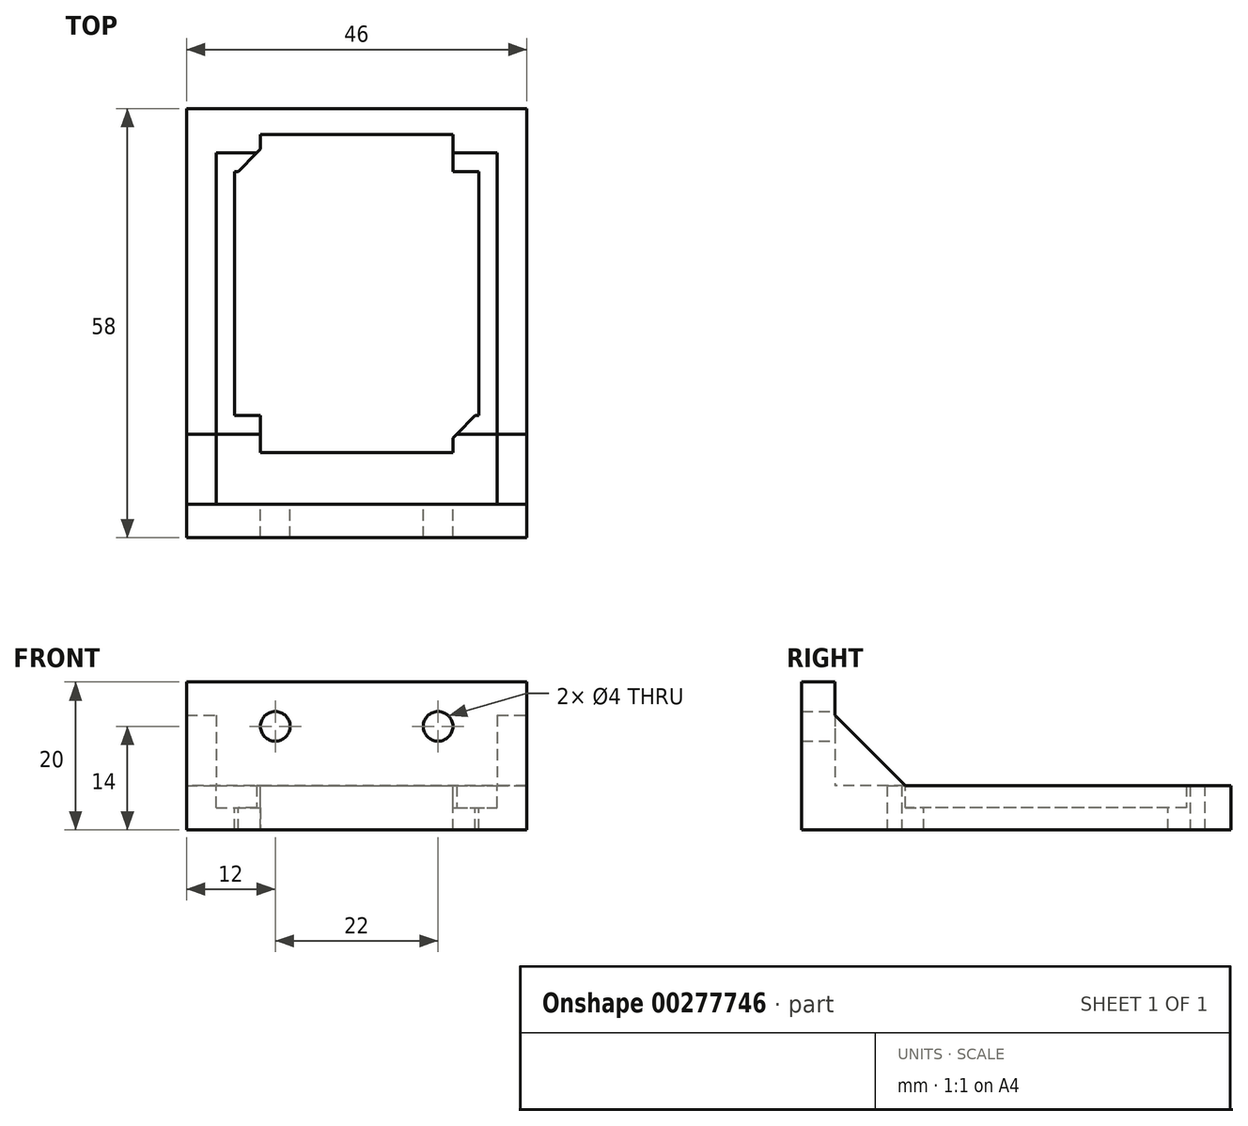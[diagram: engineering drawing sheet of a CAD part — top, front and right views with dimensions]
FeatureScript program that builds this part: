
annotation { "Feature Type Name" : "Feature", "Feature Type Description" : "" }
export const myFeature = defineFeature(function(context is Context, id is Id, definition is map)
    precondition{}
    {
        {
            var Q0;
            Q0=qCreatedBy(makeId("Top.planeOp"),FACE);
            var sketch = newSketch(context, id + "F0", { "sketchPlane" : qUnion([Q0])});
            skLineSegment(sketch, "E0.bottom", {"start": v(23, -29) * mm, "end": v(-23, -29) * mm});
            skLineSegment(sketch, "E0.top", {"start": v(23, 29) * mm, "end": v(-23, 29) * mm});
            skLineSegment(sketch, "E0.left", {"start": v(23, -29) * mm, "end": v(23, 29) * mm});
            skLineSegment(sketch, "E0.right", {"start": v(-23, -29) * mm, "end": v(-23, 29) * mm});
            skPoint(sketch, "E0.middle", {"position": v(0, 0) * mm});
            skSolve(sketch);
        }
        {
            var Q0;
            Q0 = qSketchRegion(id + "F0", true);
            extrude(context, id + "F1", {"entities" : qUnion([Q0]), "depth" : 6 * mm});
        }
        {
            var Q0;
            Q0=makeQuery(id+"F1.opExtrude","CAP_FACE",FACE,{"disambiguationData":[OSD([sQuery(id+"F0.wireOp",EDGE,"E0.bottom"),sQuery(id+"F0.wireOp",EDGE,"E0.top"),sQuery(id+"F0.wireOp",EDGE,"E0.left"),sQuery(id+"F0.wireOp",EDGE,"E0.right")])],"isStart":false});
            var sketch = newSketch(context, id + "F2", { "sketchPlane" : qUnion([Q0])});
            skLineSegment(sketch, "E1.bottom", {"start": v(-19, 23) * mm, "end": v(19, 23) * mm});
            skLineSegment(sketch, "E1.top", {"start": v(-19, -15) * mm, "end": v(19, -15) * mm});
            skLineSegment(sketch, "E1.left", {"start": v(-19, 23) * mm, "end": v(-19, -15) * mm});
            skLineSegment(sketch, "E1.right", {"start": v(19, 23) * mm, "end": v(19, -15) * mm});
            skSolve(sketch);
        }
        {
            var Q0;
            Q0 = qSketchRegion(id + "F2", true);
            extrude(context, id + "F3", {"entities" : qUnion([Q0]), "operationType" : NewBodyOperationType.REMOVE, "oppositeDirection" : true, "depth" : 3 * mm});
        }
        {
            var Q0;
            Q0=makeQuery(id+"F3.boolean.opBoolean","COPY",FACE,{"derivedFrom":makeQuery(id+"F3.opExtrude","CAP_FACE",FACE,{"disambiguationData":[OSD([sQuery(id+"F2.wireOp",EDGE,"E1.bottom"),sQuery(id+"F2.wireOp",EDGE,"E1.top"),sQuery(id+"F2.wireOp",EDGE,"E1.left"),sQuery(id+"F2.wireOp",EDGE,"E1.right")])],"isStart":false})});
            var sketch = newSketch(context, id + "F4", { "sketchPlane" : qUnion([Q0])});
            skLineSegment(sketch, "E2.bottom", {"start": v(-16.5, 20.5) * mm, "end": v(16.5, 20.5) * mm});
            skLineSegment(sketch, "E2.top", {"start": v(-16.5, -12.5) * mm, "end": v(16.5, -12.5) * mm});
            skLineSegment(sketch, "E2.left", {"start": v(-16.5, 20.5) * mm, "end": v(-16.5, -12.5) * mm});
            skLineSegment(sketch, "E2.right", {"start": v(16.5, 20.5) * mm, "end": v(16.5, -12.5) * mm});
            skSolve(sketch);
        }
        {
            var Q0;
            Q0 = qSketchRegion(id + "F4", true);
            extrude(context, id + "F5", {"entities" : qUnion([Q0]), "operationType" : NewBodyOperationType.REMOVE, "endBound" : BoundingType.THROUGH_ALL, "oppositeDirection" : true, "depth" : 25 * mm});
        }
        {
            var Q0;
            Q0=makeQuery(id+"F3.boolean.opBoolean","COPY",FACE,{"derivedFrom":makeQuery(id+"F3.opExtrude","CAP_FACE",FACE,{"disambiguationData":[OSD([sQuery(id+"F2.wireOp",EDGE,"E1.bottom"),sQuery(id+"F2.wireOp",EDGE,"E1.top"),sQuery(id+"F2.wireOp",EDGE,"E1.left"),sQuery(id+"F2.wireOp",EDGE,"E1.right")])],"isStart":false})});
            var sketch = newSketch(context, id + "F6", { "sketchPlane" : qUnion([Q0])});
            skLineSegment(sketch, "E3.bottom", {"start": v(-13, 20.5) * mm, "end": v(13, 20.5) * mm});
            skLineSegment(sketch, "E3.top", {"start": v(-13, 25.5) * mm, "end": v(13, 25.5) * mm});
            skLineSegment(sketch, "E3.left", {"start": v(-13, 20.5) * mm, "end": v(-13, 25.5) * mm});
            skLineSegment(sketch, "E3.right", {"start": v(13, 20.5) * mm, "end": v(13, 25.5) * mm});
            skSolve(sketch);
        }
        {
            var Q0;
            Q0 = qSketchRegion(id + "F6", true);
            extrude(context, id + "F7", {"entities" : qUnion([Q0]), "operationType" : NewBodyOperationType.REMOVE, "endBound" : BoundingType.THROUGH_ALL, "oppositeDirection" : true, "depth" : 25 * mm, "hasSecondDirection" : true, "secondDirectionBound" : SecondDirectionBoundingType.THROUGH_ALL, "secondDirectionOppositeDirection" : false, "secondDirectionDepth" : 25 * mm});
        }
        {
            var Q0;
            Q0=makeQuery(id+"F3.boolean.opBoolean","COPY",FACE,{"derivedFrom":makeQuery(id+"F3.opExtrude","CAP_FACE",FACE,{"disambiguationData":[OSD([sQuery(id+"F2.wireOp",EDGE,"E1.bottom"),sQuery(id+"F2.wireOp",EDGE,"E1.top"),sQuery(id+"F2.wireOp",EDGE,"E1.left"),sQuery(id+"F2.wireOp",EDGE,"E1.right")])],"isStart":false})});
            var sketch = newSketch(context, id + "F8", { "sketchPlane" : qUnion([Q0])});
            skLineSegment(sketch, "E4.bottom", {"start": v(-13, -12.5) * mm, "end": v(13, -12.5) * mm});
            skLineSegment(sketch, "E4.top", {"start": v(-13, -17.5) * mm, "end": v(13, -17.5) * mm});
            skLineSegment(sketch, "E4.left", {"start": v(-13, -12.5) * mm, "end": v(-13, -17.5) * mm});
            skLineSegment(sketch, "E4.right", {"start": v(13, -12.5) * mm, "end": v(13, -17.5) * mm});
            skSolve(sketch);
        }
        {
            var Q0;
            Q0 = qSketchRegion(id + "F8", true);
            extrude(context, id + "F9", {"entities" : qUnion([Q0]), "operationType" : NewBodyOperationType.REMOVE, "endBound" : BoundingType.THROUGH_ALL, "depth" : 25 * mm, "hasSecondDirection" : true, "secondDirectionBound" : SecondDirectionBoundingType.THROUGH_ALL, "secondDirectionOppositeDirection" : true, "secondDirectionDepth" : 25 * mm});
        }
        {
            var Q0;
            Q0=makeQuery(id+"F9.boolean.opBoolean","COPY",EDGE,{"derivedFrom":makeQuery(id+"F9.opExtrude","SWEPT_EDGE",EDGE,{"disambiguationData":[OSD([sQuery(id+"F4.wireOp",EDGE,"E2.top"),sQuery(id+"F8.wireOp",EDGE,"E4.bottom"),sQuery(id+"F8.wireOp",EDGE,"E4.left")])]})});
            var Q1;
            Q1=makeQuery(id+"F7.boolean.opBoolean","COPY",EDGE,{"derivedFrom":makeQuery(id+"F7.opExtrude","SWEPT_EDGE",EDGE,{"disambiguationData":[OSD([sQuery(id+"F4.wireOp",EDGE,"E2.bottom"),sQuery(id+"F6.wireOp",EDGE,"E3.bottom"),sQuery(id+"F6.wireOp",EDGE,"E3.left")])]})});
            var Q2;
            Q2=makeQuery(id+"F7.boolean.opBoolean","COPY",EDGE,{"derivedFrom":makeQuery(id+"F7.opExtrude","SWEPT_EDGE",EDGE,{"disambiguationData":[OSD([sQuery(id+"F4.wireOp",EDGE,"E2.bottom"),sQuery(id+"F6.wireOp",EDGE,"E3.bottom"),sQuery(id+"F6.wireOp",EDGE,"E3.right")])]})});
            var Q3;
            Q3=makeQuery(id+"F9.boolean.opBoolean","COPY",EDGE,{"derivedFrom":makeQuery(id+"F9.opExtrude","SWEPT_EDGE",EDGE,{"disambiguationData":[OSD([sQuery(id+"F4.wireOp",EDGE,"E2.top"),sQuery(id+"F8.wireOp",EDGE,"E4.bottom"),sQuery(id+"F8.wireOp",EDGE,"E4.right")])]})});
            chamfer(context, id + "F10", {"entities" : qUnion([Q0, Q1, Q2, Q3]), "width" : 3 * mm, "tangentPropagation" : true});
        }
        {
            var Q0;
            Q0=makeQuery(id+"F1.opExtrude","SWEPT_FACE",FACE,{"disambiguationData":[OSD([sQuery(id+"F0.wireOp",EDGE,"E0.right")])]});
            var sketch = newSketch(context, id + "F11", { "sketchPlane" : qUnion([Q0])});
            skLineSegment(sketch, "E5.bottom", {"start": v(29, 0) * mm, "end": v(24.5, 0) * mm});
            skLineSegment(sketch, "E5.top", {"start": v(29, 20) * mm, "end": v(24.5, 20) * mm});
            skLineSegment(sketch, "E5.left", {"start": v(29, 0) * mm, "end": v(29, 20) * mm});
            skLineSegment(sketch, "E5.right", {"start": v(24.5, 0) * mm, "end": v(24.5, 20) * mm});
            skSolve(sketch);
        }
        {
            var Q0;
            Q0 = qSketchRegion(id + "F11", true);
            extrude(context, id + "F12", {"entities" : qUnion([Q0]), "operationType" : NewBodyOperationType.ADD, "oppositeDirection" : true, "depth" : 46 * mm});
        }
        {
            var Q0;
            Q0=makeQuery(id+"F1.opExtrude","CAP_FACE",FACE,{"disambiguationData":[OSD([sQuery(id+"F0.wireOp",EDGE,"E0.bottom"),sQuery(id+"F0.wireOp",EDGE,"E0.top"),sQuery(id+"F0.wireOp",EDGE,"E0.left"),sQuery(id+"F0.wireOp",EDGE,"E0.right")])],"isStart":false});
            var sketch = newSketch(context, id + "F13", { "sketchPlane" : qUnion([Q0])});
            skLineSegment(sketch, "E6.bottom", {"start": v(-23, -24.5) * mm, "end": v(-19, -24.5) * mm});
            skLineSegment(sketch, "E6.top", {"start": v(-23, -15) * mm, "end": v(-19, -15) * mm});
            skLineSegment(sketch, "E6.left", {"start": v(-23, -24.5) * mm, "end": v(-23, -15) * mm});
            skLineSegment(sketch, "E6.right", {"start": v(-19, -24.5) * mm, "end": v(-19, -15) * mm});
            skSolve(sketch);
        }
        {
            var Q0;
            Q0 = qSketchRegion(id + "F13", true);
            extrude(context, id + "F14", {"entities" : qUnion([Q0]), "operationType" : NewBodyOperationType.ADD, "depth" : 10 * mm});
        }
        {
            var Q0;
            Q0=makeQuery(id+"F14.opExtrude","CAP_EDGE",EDGE,{"disambiguationData":[OSD([sQuery(id+"F13.wireOp",EDGE,"E6.top")])],"isStart":false});
            chamfer(context, id + "F15", {"entities" : qUnion([Q0]), "width" : 10 * mm, "tangentPropagation" : true});
        }
        {
            var Q0;
            Q0=makeQuery(id+"F1.opExtrude","CAP_FACE",FACE,{"disambiguationData":[OSD([sQuery(id+"F0.wireOp",EDGE,"E0.bottom"),sQuery(id+"F0.wireOp",EDGE,"E0.top"),sQuery(id+"F0.wireOp",EDGE,"E0.left"),sQuery(id+"F0.wireOp",EDGE,"E0.right")])],"isStart":false});
            var sketch = newSketch(context, id + "F16", { "sketchPlane" : qUnion([Q0])});
            skLineSegment(sketch, "E7.bottom", {"start": v(19, -15) * mm, "end": v(23, -15) * mm});
            skLineSegment(sketch, "E7.top", {"start": v(19, -24.5) * mm, "end": v(23, -24.5) * mm});
            skLineSegment(sketch, "E7.left", {"start": v(19, -15) * mm, "end": v(19, -24.5) * mm});
            skLineSegment(sketch, "E7.right", {"start": v(23, -15) * mm, "end": v(23, -24.5) * mm});
            skSolve(sketch);
        }
        {
            var Q0;
            Q0 = qSketchRegion(id + "F16", true);
            extrude(context, id + "F17", {"entities" : qUnion([Q0]), "operationType" : NewBodyOperationType.ADD, "depth" : 10 * mm});
        }
        {
            var Q0;
            Q0=makeQuery(id+"F17.opExtrude","CAP_EDGE",EDGE,{"disambiguationData":[OSD([sQuery(id+"F16.wireOp",EDGE,"E7.bottom")])],"isStart":false});
            chamfer(context, id + "F18", {"entities" : qUnion([Q0]), "width" : 10 * mm, "tangentPropagation" : true});
        }
        {
            var Q0;
            Q0=makeQuery(id+"F12.opExtrude","SWEPT_FACE",FACE,{"disambiguationData":[OSD([sQuery(id+"F11.wireOp",EDGE,"E5.right")])]});
            var sketch = newSketch(context, id + "F19", { "sketchPlane" : qUnion([Q0])});
            skCircle(sketch, "E8", {"center": v(11, 14) * mm, "radius": 2 * mm});
            skCircle(sketch, "E9.MirrorC", {"center": v(-11, 14) * mm, "radius": 2 * mm});
            skSolve(sketch);
        }
        {
            var Q0;
            Q0 = qSketchRegion(id + "F19", true);
            extrude(context, id + "F20", {"entities" : qUnion([Q0]), "operationType" : NewBodyOperationType.REMOVE, "endBound" : BoundingType.THROUGH_ALL, "oppositeDirection" : true, "depth" : 25 * mm});
        }
    });
